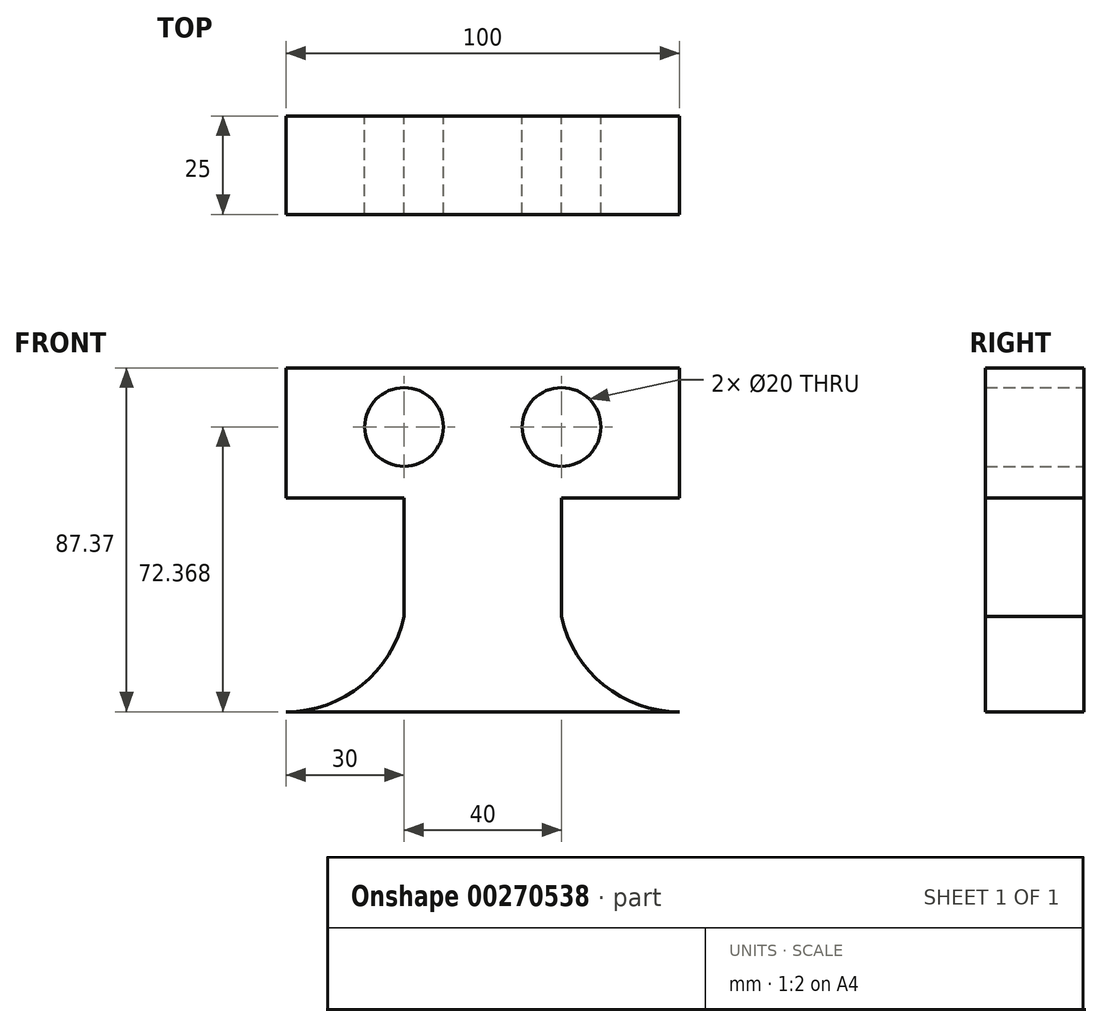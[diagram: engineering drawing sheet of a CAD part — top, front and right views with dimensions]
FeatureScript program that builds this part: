
annotation { "Feature Type Name" : "Feature", "Feature Type Description" : "" }
export const myFeature = defineFeature(function(context is Context, id is Id, definition is map)
    precondition{}
    {
        {
            var Q0;
            Q0=qCreatedBy(makeId("Front.planeOp"),FACE);
            var sketch = newSketch(context, id + "F0", { "sketchPlane" : qUnion([Q0])});
            skLineSegment(sketch, "E0", {"start": v(-50, -46.08) * mm, "end": v(50, -46.08) * mm});
            skLineSegment(sketch, "E1", {"start": v(20, -21.81) * mm, "end": v(20, 8.19) * mm});
            skLineSegment(sketch, "E2.MirrorCS", {"start": v(-20, -21.81) * mm, "end": v(-20, 8.19) * mm});
            skLineSegment(sketch, "E3", {"start": v(-50, 41.29) * mm, "end": v(50, 41.29) * mm});
            skCircle(sketch, "E4", {"center": v(20, 26.29) * mm, "radius": 10 * mm});
            skPoint(sketch, "E4.first.point", {"position": v(12, 20.28) * mm});
            skPoint(sketch, "E4.second.point", {"position": v(28.97, 30.71) * mm});
            skPoint(sketch, "E4.third.point", {"position": v(11.03, 30.71) * mm});
            skCircle(sketch, "E5", {"center": v(-20, 26.29) * mm, "radius": 10 * mm});
            skLineSegment(sketch, "E6", {"start": v(-20, 8.19) * mm, "end": v(-50, 8.19) * mm});
            skLineSegment(sketch, "E7", {"start": v(20, 8.19) * mm, "end": v(50, 8.19) * mm});
            skLineSegment(sketch, "E8", {"start": v(50, 41.29) * mm, "end": v(50, 8.19) * mm});
            skLineSegment(sketch, "E9", {"start": v(-50, 41.29) * mm, "end": v(-50, 8.19) * mm});
            skArc(sketch, "E10", {"start": v(20, -21.81) * mm, "mid": v(30.7, -39.25) * mm, "end": v(50, -46.08) * mm});
            skArc(sketch, "E11", {"start": v(-50, -46.08) * mm, "mid": v(-30.7, -39.25) * mm, "end": v(-20, -21.81) * mm});
            skSolve(sketch);
        }
        {
            var Q0;
            Q0=makeQuery(id+"F0.imprint","IMPRINT",FACE,{"disambiguationData":[TD([[makeQuery(id+"F0.imprint","IMPRINT",EDGE,{"derivedFrom":sQuery(id+"F0.wireOp",EDGE,"E0")}),1.0]])]});
            extrude(context, id + "F1", {"entities" : qUnion([Q0]), "depth" : 25 * mm});
        }
        {
            var Q0;
            Q0=makeQuery(id+"F1.opExtrude","SWEPT_FACE",FACE,{"disambiguationData":[OSD([sQuery(id+"F0.wireOp",EDGE,"E3")])]});
            var Q1;
            Q1=sQuery(id+"F0.wireOp",EDGE,"E1");
            extrude(context, id + "F2", {"entities" : qUnion([Q0]), "bodyType" : ToolBodyType.SURFACE, "operationType" : NewBodyOperationType.ADD, "surfaceEntities" : qUnion([Q1]), "depth" : 25 * mm});
        }
    });
